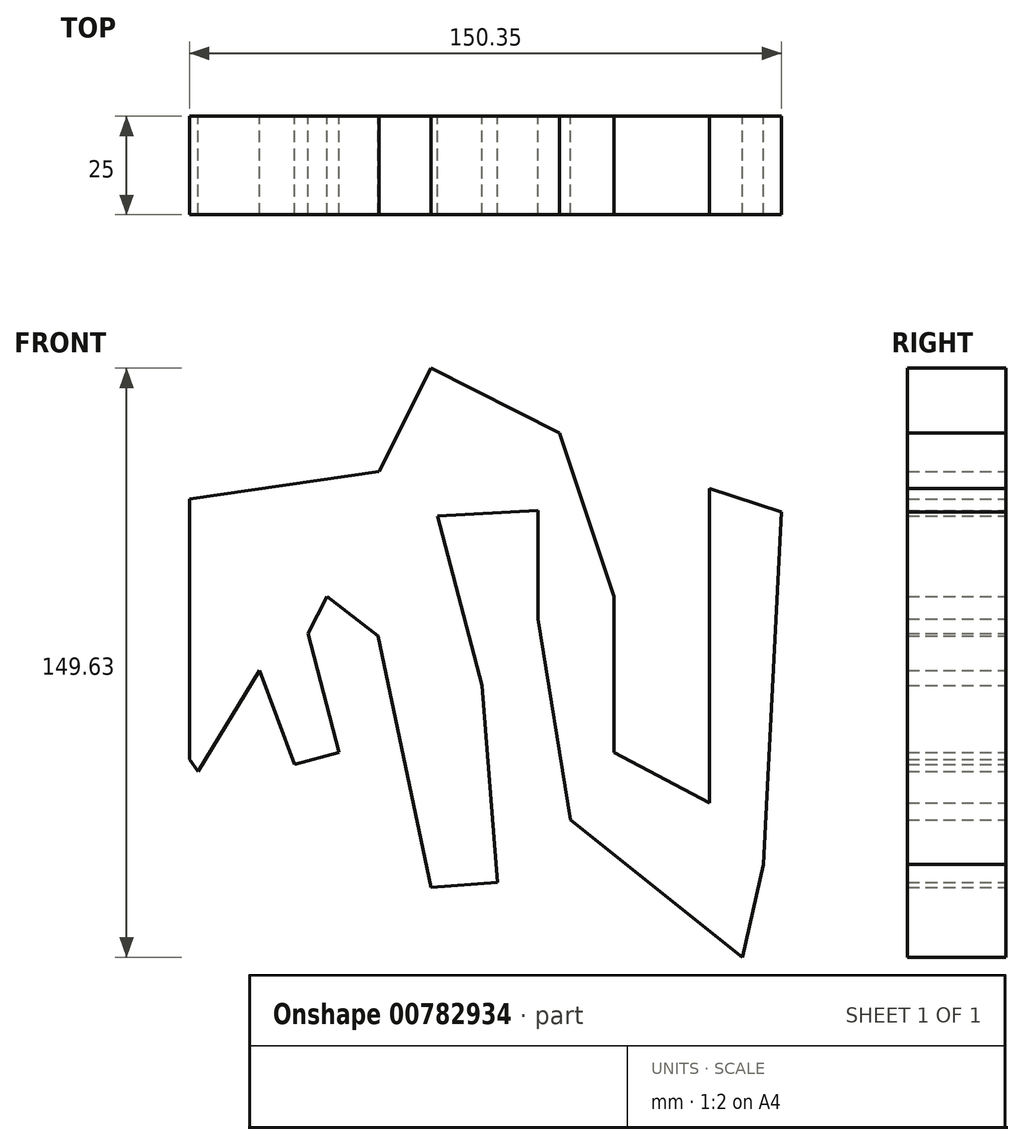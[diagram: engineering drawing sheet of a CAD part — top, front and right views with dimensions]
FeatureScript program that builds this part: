
annotation { "Feature Type Name" : "Feature", "Feature Type Description" : "" }
export const myFeature = defineFeature(function(context is Context, id is Id, definition is map)
    precondition{}
    {
        {
            var Q0;
            Q0=qCreatedBy(makeId("Front.planeOp"),FACE);
            var sketch = newSketch(context, id + "F0", { "sketchPlane" : qUnion([Q0])});
            skLineSegment(sketch, "E0", {"start": v(-61.34, -41.38) * mm, "end": v(-61.34, 24.78) * mm});
            skLineSegment(sketch, "E1", {"start": v(-61.34, 24.78) * mm, "end": v(-13.23, 31.75) * mm});
            skLineSegment(sketch, "E2", {"start": v(-13.23, 31.75) * mm, "end": v(0, 57.98) * mm});
            skLineSegment(sketch, "E3", {"start": v(0, 57.98) * mm, "end": v(32.68, 41.48) * mm});
            skLineSegment(sketch, "E4", {"start": v(32.68, 41.48) * mm, "end": v(46.43, 0) * mm});
            skLineSegment(sketch, "E5", {"start": v(46.43, 0) * mm, "end": v(46.43, -39.7) * mm});
            skLineSegment(sketch, "E6", {"start": v(46.43, -39.7) * mm, "end": v(70.73, -52.44) * mm});
            skLineSegment(sketch, "E7", {"start": v(70.73, -52.44) * mm, "end": v(70.73, 0) * mm});
            skLineSegment(sketch, "E8", {"start": v(70.73, 0) * mm, "end": v(70.73, 27.42) * mm});
            skLineSegment(sketch, "E9", {"start": v(70.73, 27.42) * mm, "end": v(89, 21.41) * mm});
            skLineSegment(sketch, "E10", {"start": v(89, 21.41) * mm, "end": v(84.44, -68.08) * mm});
            skLineSegment(sketch, "E11", {"start": v(84.44, -68.08) * mm, "end": v(79.15, -91.65) * mm});
            skLineSegment(sketch, "E12", {"start": v(79.15, -91.65) * mm, "end": v(35.36, -56.77) * mm});
            skLineSegment(sketch, "E13", {"start": v(35.36, -56.77) * mm, "end": v(27.18, -5.77) * mm});
            skLineSegment(sketch, "E14", {"start": v(27.18, -5.77) * mm, "end": v(27.18, 21.9) * mm});
            skLineSegment(sketch, "E15", {"start": v(27.18, 21.9) * mm, "end": v(1.68, 20.45) * mm});
            skLineSegment(sketch, "E16", {"start": v(1.68, 20.45) * mm, "end": v(13, -22.61) * mm});
            skLineSegment(sketch, "E17", {"start": v(13, -22.61) * mm, "end": v(16.84, -72.65) * mm});
            skLineSegment(sketch, "E18", {"start": v(16.84, -72.65) * mm, "end": v(0, -73.95) * mm});
            skLineSegment(sketch, "E19", {"start": v(0, -73.95) * mm, "end": v(-13.47, -10.1) * mm});
            skLineSegment(sketch, "E20", {"start": v(-13.47, -10.1) * mm, "end": v(-26.46, 0) * mm});
            skLineSegment(sketch, "E21", {"start": v(-26.46, 0) * mm, "end": v(-31.27, -9.38) * mm});
            skLineSegment(sketch, "E22", {"start": v(-31.27, -9.38) * mm, "end": v(-23.33, -39.7) * mm});
            skLineSegment(sketch, "E23", {"start": v(-23.33, -39.7) * mm, "end": v(-34.72, -42.67) * mm});
            skLineSegment(sketch, "E24", {"start": v(-34.72, -42.67) * mm, "end": v(-43.54, -18.76) * mm});
            skLineSegment(sketch, "E25", {"start": v(-43.54, -18.76) * mm, "end": v(-59.18, -44.5) * mm});
            skLineSegment(sketch, "E26", {"start": v(-59.18, -44.5) * mm, "end": v(-61.34, -41.38) * mm});
            skSolve(sketch);
        }
        {
            var Q0;
            Q0 = qSketchRegion(id + "F0", true);
            extrude(context, id + "F1", {"entities" : qUnion([Q0]), "depth" : 25 * mm, "offsetDistance" : 25 * mm});
        }
    });
